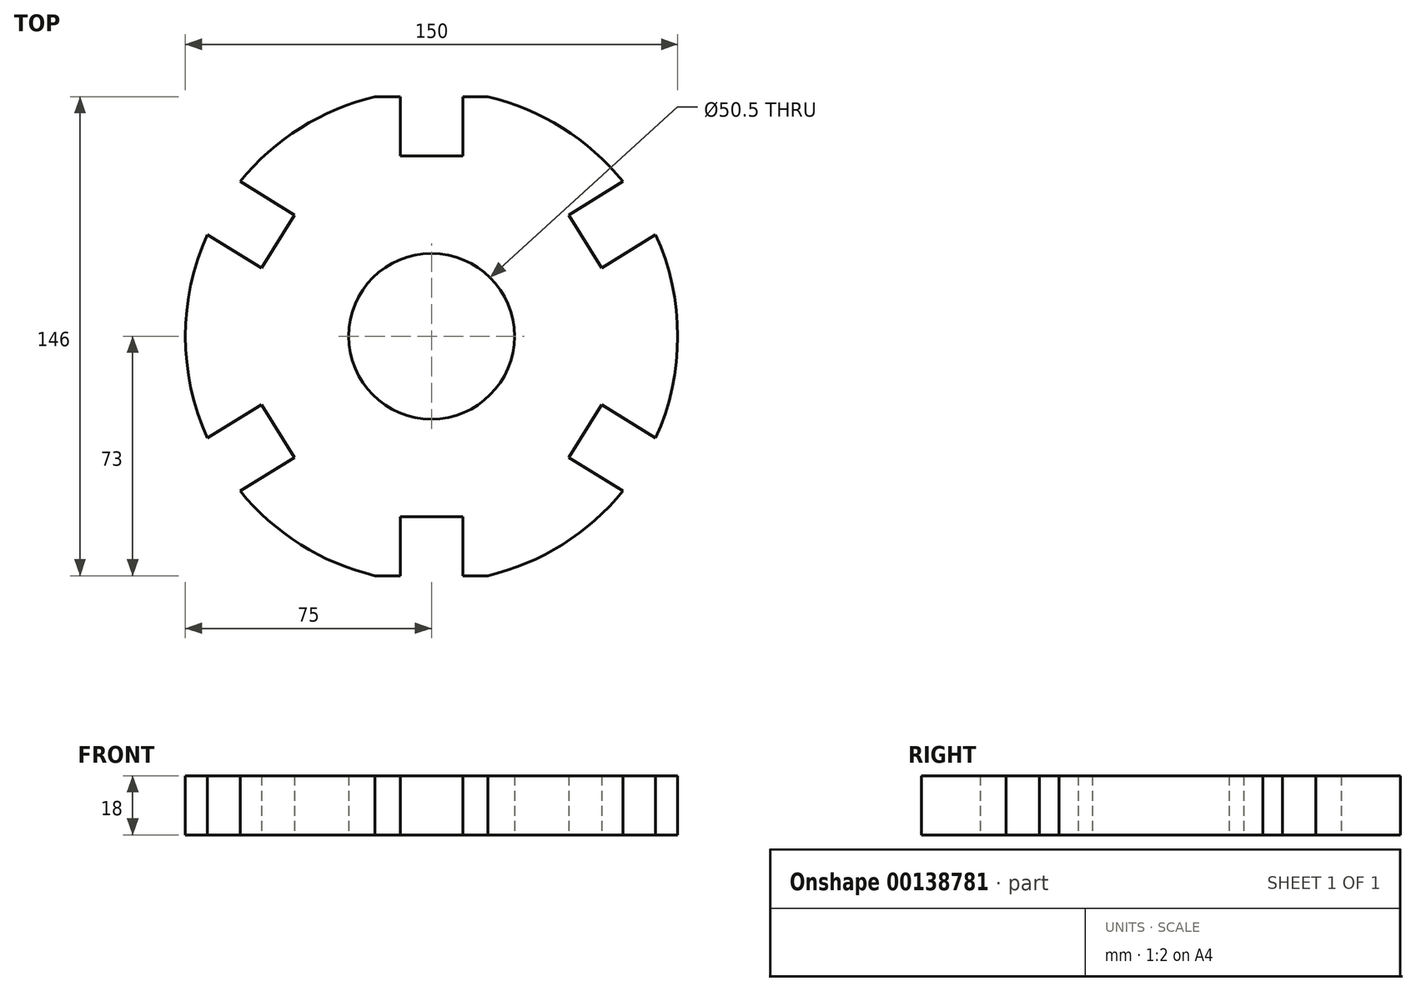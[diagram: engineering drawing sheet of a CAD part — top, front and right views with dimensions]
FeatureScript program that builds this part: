
annotation { "Feature Type Name" : "Feature", "Feature Type Description" : "" }
export const myFeature = defineFeature(function(context is Context, id is Id, definition is map)
    precondition{}
    {
        {
            var Q0;
            Q0=qCreatedBy(makeId("Top.planeOp"),FACE);
            var sketch = newSketch(context, id + "F0", { "sketchPlane" : qUnion([Q0])});
            skCircle(sketch, "E0", {"center": v(0, 0) * mm, "radius": 25.25 * mm});
            skArc(sketch, "E1", {"start": v(-17.2, 73) * mm, "mid": v(-39.9, 63.5) * mm, "end": v(-58.3, 47.18) * mm});
            skLineSegment(sketch, "E2.bottom", {"start": v(9.5, 55) * mm, "end": v(-9.5, 55) * mm});
            skLineSegment(sketch, "E2.left", {"start": v(9.5, 55) * mm, "end": v(9.5, 73) * mm});
            skLineSegment(sketch, "E2.right", {"start": v(-9.5, 55) * mm, "end": v(-9.5, 73) * mm});
            skLineSegment(sketch, "E3", {"start": v(0, 0) * mm, "end": v(46.8, 28.9) * mm, "construction": true});
            skLineSegment(sketch, "E4", {"start": v(41.8, 36.98) * mm, "end": v(58.3, 47.18) * mm});
            skLineSegment(sketch, "E5.MirrorCS", {"start": v(51.79, 20.82) * mm, "end": v(68.29, 31.01) * mm});
            skLineSegment(sketch, "E6", {"start": v(41.8, 36.98) * mm, "end": v(51.79, 20.82) * mm});
            skArc(sketch, "E7.trimOffspring", {"start": v(58.3, 47.18) * mm, "mid": v(39.9, 63.5) * mm, "end": v(17.2, 73) * mm});
            skLineSegment(sketch, "E8.MirrorCS", {"start": v(51.79, 20.82) * mm, "end": v(41.8, 36.98) * mm});
            skLineSegment(sketch, "E9.MirrorCS", {"start": v(-41.8, 36.98) * mm, "end": v(-51.79, 20.82) * mm});
            skLineSegment(sketch, "E10.MirrorCS", {"start": v(-51.79, 20.82) * mm, "end": v(-41.8, 36.98) * mm});
            skLineSegment(sketch, "E11.MirrorCS", {"start": v(-51.79, 20.82) * mm, "end": v(-68.29, 31.01) * mm});
            skLineSegment(sketch, "E12.MirrorCS", {"start": v(-41.8, 36.98) * mm, "end": v(-58.3, 47.18) * mm});
            skArc(sketch, "E13.trimOffspring", {"start": v(17.2, 73) * mm, "mid": v(39.9, 63.5) * mm, "end": v(58.3, 47.18) * mm});
            skLineSegment(sketch, "E14.MirrorCS", {"start": v(41.8, -36.98) * mm, "end": v(51.79, -20.82) * mm});
            skLineSegment(sketch, "E15.MirrorCS", {"start": v(-51.79, -20.82) * mm, "end": v(-68.29, -31.01) * mm});
            skLineSegment(sketch, "E16.MirrorCS", {"start": v(41.8, -36.98) * mm, "end": v(58.3, -47.18) * mm});
            skLineSegment(sketch, "E17.MirrorCS", {"start": v(-41.8, -36.98) * mm, "end": v(-58.3, -47.18) * mm});
            skLineSegment(sketch, "E18.MirrorCS", {"start": v(51.79, -20.82) * mm, "end": v(41.8, -36.98) * mm});
            skLineSegment(sketch, "E19.MirrorCS", {"start": v(51.79, -20.82) * mm, "end": v(68.29, -31.01) * mm});
            skLineSegment(sketch, "E20.MirrorCS", {"start": v(-41.8, -36.98) * mm, "end": v(-51.79, -20.82) * mm});
            skLineSegment(sketch, "E21.MirrorCS", {"start": v(-51.79, -20.82) * mm, "end": v(-41.8, -36.98) * mm});
            skLineSegment(sketch, "E22.MirrorCS", {"start": v(9.5, -55) * mm, "end": v(-9.5, -55) * mm});
            skLineSegment(sketch, "E23.MirrorCS", {"start": v(9.5, -55) * mm, "end": v(9.5, -73) * mm});
            skLineSegment(sketch, "E24.MirrorCS", {"start": v(-9.5, -55) * mm, "end": v(-9.5, -73) * mm});
            skArc(sketch, "E25.trimOffspring", {"start": v(-58.3, -47.18) * mm, "mid": v(-39.9, -63.5) * mm, "end": v(-17.2, -73) * mm});
            skArc(sketch, "E26.trimOffspring", {"start": v(68.29, -31.01) * mm, "mid": v(75, 0) * mm, "end": v(68.29, 31.01) * mm});
            skArc(sketch, "E27.trimOffspring", {"start": v(17.2, -73) * mm, "mid": v(39.9, -63.5) * mm, "end": v(58.3, -47.18) * mm});
            skArc(sketch, "E28.trimOffspring", {"start": v(-68.29, -31.01) * mm, "mid": v(-75, 0) * mm, "end": v(-68.29, 31.01) * mm});
            skLineSegment(sketch, "E29", {"start": v(-17.2, 73) * mm, "end": v(-9.5, 73) * mm});
            skLineSegment(sketch, "E30.trimOffspring", {"start": v(9.5, 73) * mm, "end": v(17.2, 73) * mm});
            skLineSegment(sketch, "E31.MirrorCS", {"start": v(-17.2, -73) * mm, "end": v(-9.5, -73) * mm});
            skLineSegment(sketch, "E32.MirrorCS", {"start": v(9.5, -73) * mm, "end": v(17.2, -73) * mm});
            skSolve(sketch);
        }
        {
            var Q0;
            Q0=makeQuery(id+"F0.imprint","IMPRINT",FACE,{"disambiguationData":[TD([[makeQuery(id+"F0.imprint","IMPRINT",EDGE,{"derivedFrom":sQuery(id+"F0.wireOp",EDGE,"E0")}),-1.0]])]});
            extrude(context, id + "F1", {"entities" : qUnion([Q0]), "depth" : 18 * mm});
        }
    });
